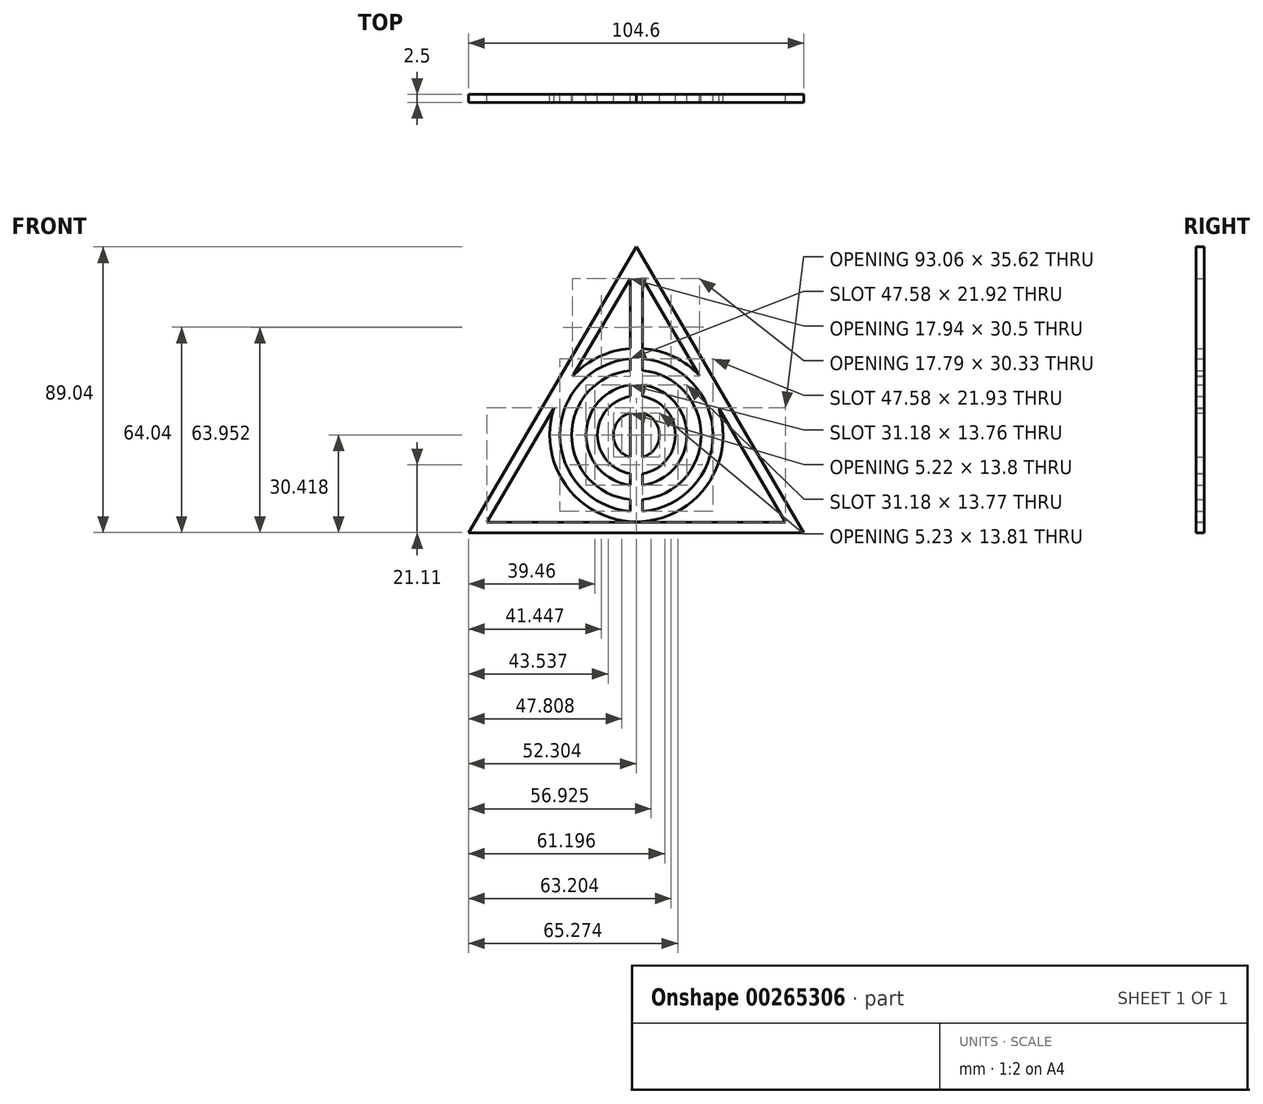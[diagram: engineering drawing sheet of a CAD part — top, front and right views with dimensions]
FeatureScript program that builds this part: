
annotation { "Feature Type Name" : "Feature", "Feature Type Description" : "" }
export const myFeature = defineFeature(function(context is Context, id is Id, definition is map)
    precondition{}
    {
        {
            var Q0;
            Q0=qCreatedBy(makeId("Front.planeOp"),FACE);
            var sketch = newSketch(context, id + "F0", { "sketchPlane" : qUnion([Q0])});
            skLineSegment(sketch, "E0", {"start": v(0, 62.65) * mm, "end": v(-52.37, -26.4) * mm});
            skLineSegment(sketch, "E1", {"start": v(-52.37, -26.4) * mm, "end": v(52.23, -26.4) * mm});
            skLineSegment(sketch, "E2", {"start": v(52.23, -26.4) * mm, "end": v(0, 62.65) * mm});
            skLineSegment(sketch, "E3.0", {"start": v(46.46, -23.1) * mm, "end": v(0, 56.13) * mm});
            skLineSegment(sketch, "E3.1", {"start": v(-46.6, -23.1) * mm, "end": v(46.46, -23.1) * mm});
            skLineSegment(sketch, "E3.2", {"start": v(0, 56.13) * mm, "end": v(-46.6, -23.1) * mm});
            skLineSegment(sketch, "E4", {"start": v(-1.95, 52.81) * mm, "end": v(-1.95, -23.1) * mm});
            skLineSegment(sketch, "E5", {"start": v(1.94, 52.81) * mm, "end": v(1.94, -23.1) * mm});
            skArc(sketch, "E6", {"start": v(-25.65, 12.53) * mm, "mid": v(-0.15, -22.99) * mm, "end": v(25.74, 12.24) * mm});
            skArc(sketch, "E7.0", {"start": v(-1.95, 27.82) * mm, "mid": v(-23.87, 4.03) * mm, "end": v(-1.95, -19.76) * mm});
            skArc(sketch, "E8.0", {"start": v(-1.95, 24.12) * mm, "mid": v(-20.18, 4.03) * mm, "end": v(-1.95, -16.06) * mm});
            skArc(sketch, "E9.0", {"start": v(-1.95, 19.62) * mm, "mid": v(-15.71, 4.03) * mm, "end": v(-1.95, -11.56) * mm});
            skArc(sketch, "E10.0", {"start": v(-1.95, 16.03) * mm, "mid": v(-12.16, 4.03) * mm, "end": v(-1.95, -7.97) * mm});
            skArc(sketch, "E11.trimOffspring", {"start": v(19.73, 22.49) * mm, "mid": v(11.64, 28.41) * mm, "end": v(1.94, 30.98) * mm});
            skArc(sketch, "E12.trimOffspring", {"start": v(-1.95, 30.98) * mm, "mid": v(-11.75, 28.36) * mm, "end": v(-19.9, 22.31) * mm});
            skArc(sketch, "E13.trimOffspring", {"start": v(1.94, -19.76) * mm, "mid": v(23.87, 4.03) * mm, "end": v(1.94, 27.82) * mm});
            skArc(sketch, "E14.trimOffspring", {"start": v(1.94, -16.06) * mm, "mid": v(20.18, 4.03) * mm, "end": v(1.94, 24.12) * mm});
            skArc(sketch, "E15.trimOffspring", {"start": v(1.94, -11.56) * mm, "mid": v(15.71, 4.03) * mm, "end": v(1.94, 19.62) * mm});
            skArc(sketch, "E16.trimOffspring", {"start": v(1.94, -7.98) * mm, "mid": v(12.16, 4.03) * mm, "end": v(1.94, 16.03) * mm});
            skArc(sketch, "E17", {"start": v(-1.95, 10.93) * mm, "mid": v(-7.17, 4.03) * mm, "end": v(-1.95, -2.87) * mm});
            skArc(sketch, "E18.trimOffspring", {"start": v(1.94, -2.88) * mm, "mid": v(7.17, 4.03) * mm, "end": v(1.94, 10.93) * mm});
            skSolve(sketch);
        }
        {
            var Q0;
            {var subQ0=sQuery(id+"F0.wireOp",EDGE,"E7.0");Q0=makeQuery(id+"F0.imprint","IMPRINT",FACE,{"disambiguationData":[TD([[makeQuery(id+"F0.imprint","IMPRINT",EDGE,{"derivedFrom":subQ0}),-1.0]])]});}
            var Q1;
            {var subQ6=sQuery(id+"F0.wireOp",EDGE,"E11.trimOffspring");Q1=makeQuery(id+"F0.imprint","IMPRINT",FACE,{"disambiguationData":[TD([[makeQuery(id+"F0.imprint","IMPRINT",EDGE,{"derivedFrom":subQ6}),1.0]])]});}
            var Q2;
            {var subQ5=sQuery(id+"F0.wireOp",EDGE,"E3.0");var subQ24=sQuery(id+"F0.wireOp",EDGE,"E3.2");var subQ31=makeQuery(id+"F0.imprint","INTERSECT",VERTEX,{"derivedFrom":[subQ5,subQ24]});Q2=makeQuery(id+"F0.imprint","IMPRINT",FACE,{"disambiguationData":[TD([[makeQuery(id+"F0.imprint","IMPRINT",EDGE,{"disambiguationData":[TD([[subQ31,1.0]])],"derivedFrom":subQ5}),1.0]])]});}
            var Q3;
            {var subQ0=sQuery(id+"F0.wireOp",EDGE,"E8.0");Q3=makeQuery(id+"F0.imprint","IMPRINT",FACE,{"disambiguationData":[TD([[makeQuery(id+"F0.imprint","IMPRINT",EDGE,{"derivedFrom":subQ0}),1.0]])]});}
            var Q4;
            {var subQ0=sQuery(id+"F0.wireOp",EDGE,"E14.trimOffspring");Q4=makeQuery(id+"F0.imprint","IMPRINT",FACE,{"disambiguationData":[TD([[makeQuery(id+"F0.imprint","IMPRINT",EDGE,{"derivedFrom":subQ0}),1.0]])]});}
            var Q5;
            Q5=makeQuery(id+"F0.imprint","IMPRINT",FACE,{"disambiguationData":[TD([[makeQuery(id+"F0.imprint","IMPRINT",EDGE,{"derivedFrom":sQuery(id+"F0.wireOp",EDGE,"E0")}),1.0]])]});
            var Q6;
            {var subQ0=sQuery(id+"F0.wireOp",EDGE,"E10.0");Q6=makeQuery(id+"F0.imprint","IMPRINT",FACE,{"disambiguationData":[TD([[makeQuery(id+"F0.imprint","IMPRINT",EDGE,{"derivedFrom":subQ0}),1.0]])]});}
            var Q7;
            {var subQ0=sQuery(id+"F0.wireOp",EDGE,"E16.trimOffspring");Q7=makeQuery(id+"F0.imprint","IMPRINT",FACE,{"disambiguationData":[TD([[makeQuery(id+"F0.imprint","IMPRINT",EDGE,{"derivedFrom":subQ0}),1.0]])]});}
            extrude(context, id + "F1", {"entities" : qUnion([Q0, Q1, Q2, Q3, Q4, Q5, Q6, Q7]), "depth" : 2.5 * mm});
        }
    });
